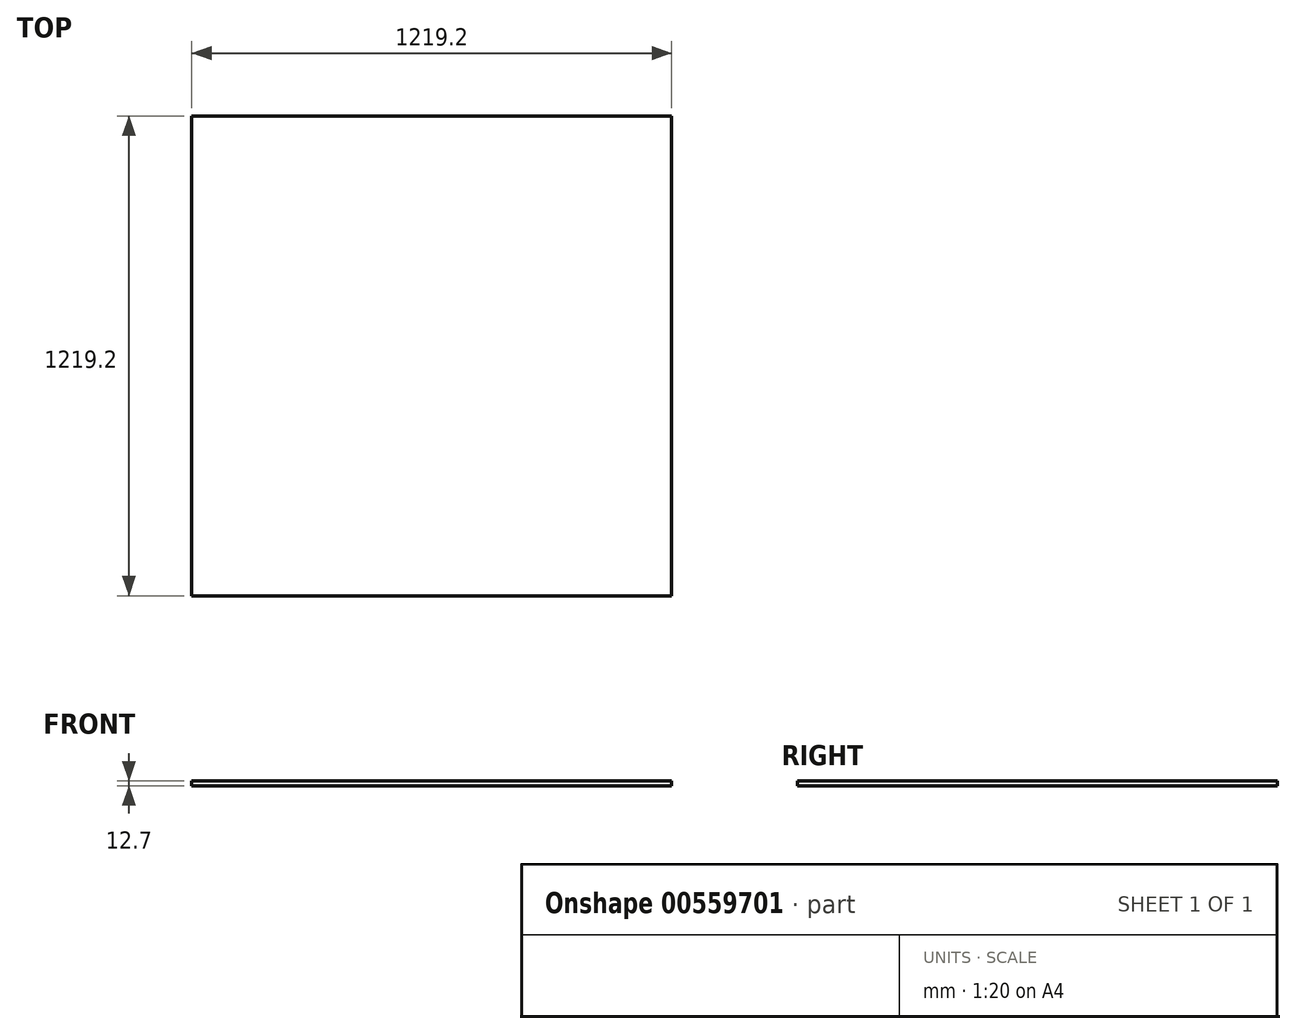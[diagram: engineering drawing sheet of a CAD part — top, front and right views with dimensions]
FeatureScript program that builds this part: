
annotation { "Feature Type Name" : "Feature", "Feature Type Description" : "" }
export const myFeature = defineFeature(function(context is Context, id is Id, definition is map)
    precondition{}
    {
        {
            var Q0;
            Q0=qCreatedBy(makeId("Top.planeOp"),FACE);
            var sketch = newSketch(context, id + "F0", { "sketchPlane" : qUnion([Q0])});
            skLineSegment(sketch, "E0.bottom", {"start": v(609.6, -609.6) * mm, "end": v(-609.6, -609.6) * mm});
            skLineSegment(sketch, "E0.top", {"start": v(609.6, 609.6) * mm, "end": v(-609.6, 609.6) * mm});
            skLineSegment(sketch, "E0.left", {"start": v(609.6, -609.6) * mm, "end": v(609.6, 609.6) * mm});
            skLineSegment(sketch, "E0.right", {"start": v(-609.6, -609.6) * mm, "end": v(-609.6, 609.6) * mm});
            skPoint(sketch, "E0.middle", {"position": v(0, 0) * mm});
            skSolve(sketch);
        }
        {
            var Q0;
            Q0 = qSketchRegion(id + "F0", true);
            extrude(context, id + "F1", {"entities" : qUnion([Q0]), "depth" : 12.7 * mm, "offsetDistance" : 25.4 * mm});
        }
    });
